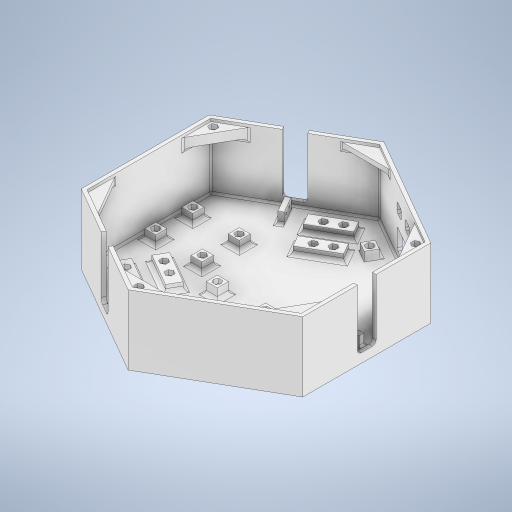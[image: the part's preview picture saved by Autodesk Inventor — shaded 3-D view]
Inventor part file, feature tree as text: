
AUTODESK INVENTOR PART (.ipt)
format: ipt  version: 2023 (Build 270158000, 158)  size: 2,672,128 bytes
history: native  units: mm
features: extrude x37, sketch x32, fillet x14, mirror x3, other x1
ambient origin geometry x8: Origin, YZ Plane, XZ Plane, XY Plane, X Axis, Y Axis, Z Axis, Center Point
bodies: Body1 (feature_tree)
feature tree (87):
  other  "Bryła1"
  extrude  "Wyciągnięcie proste1"  Depth=239.0mm
  sketch  "Szkic2"
  extrude  "Wyciągnięcie proste3"  Depth=5.0mm TaperAngle=0.0deg
  extrude  "Wyciągnięcie proste5"  Depth=4.0mm
  extrude  "Wyciągnięcie proste6"  Depth=20.0mm
  sketch  "Szkic3"
  extrude  "Wyciągnięcie proste7"  Depth=10.0mm
  extrude  "Wyciągnięcie proste9"  Depth=40.0mm
  extrude  "Wyciągnięcie proste10"  Depth=20.0mm
  mirror  "Odbij2"
  mirror  "Odbij3"
  extrude  "Wyciągnięcie proste11"  Depth=20.0mm
  extrude  "Wyciągnięcie proste12"  Depth=10.0mm
  extrude  "Wyciągnięcie proste13"  Depth=20.0mm
  extrude  "Wyciągnięcie proste16"  Depth=10.0mm
  extrude  "Wyciągnięcie proste17"  Depth=20.0mm
  extrude  "Wyciągnięcie proste18"  Depth=40.0mm
  extrude  "Wyciągnięcie proste22"  Depth=40.0mm
  extrude  "Wyciągnięcie proste23"  Depth=20.0mm
  extrude  "Wyciągnięcie proste24"  Depth=70.0mm TaperAngle=0.0deg
  extrude  "Wyciągnięcie proste25"  Depth=5.0mm TaperAngle=0.0deg
  extrude  "Wyciągnięcie proste28"  Depth=70.0mm TaperAngle=0.0deg
  extrude  "Wyciągnięcie proste29"  Depth=15.0mm
  fillet  "Zaokrąglenie1"  Radius=8.0mm
  fillet  "Zaokrąglenie2"  [1 undecoded]
  fillet  "Zaokrąglenie4"  Radius=15.0mm
  fillet  "Zaokrąglenie5"  Radius=8.0mm
  extrude  "Wyciągnięcie proste30"  Depth=3.0mm TaperAngle=0.0deg
  mirror  "Odbij4"
  extrude  "Wyciągnięcie proste31"  Depth=50.0mm
  extrude  "Wyciągnięcie proste32"  Depth=50.0mm
  extrude  "Wyciągnięcie proste33"  Depth=50.0mm
  fillet  "Zaokrąglenie6"  Radius=50.0mm
  fillet  "Zaokrąglenie7"  Radius=50.0mm
  fillet  "Zaokrąglenie8"  Radius=50.0mm
  fillet  "Zaokrąglenie9"  Radius=14.0mm
  extrude  "Wyciągnięcie proste34"  Depth=40.0mm
  extrude  "Wyciągnięcie proste35"  Depth=3.0mm
  fillet  "Zaokrąglenie10"  Radius=14.0mm
  fillet  "Zaokrąglenie11"  Radius=40.0mm
  extrude  "Wyciągnięcie proste36"  Depth=3.0mm
  extrude  "Wyciągnięcie proste37"  Depth=5.0mm
  extrude  "Wyciągnięcie proste38"  Depth=5.0mm
  fillet  "Zaokrąglenie12"  Radius=8.0mm
  extrude  "Wyciągnięcie proste39"  Depth=14.0mm
  sketch  "Szkic45"
  extrude  "Wyciągnięcie proste40"  Depth=14.0mm
  extrude  "Wyciągnięcie proste41"  Depth=5.0mm
  fillet  "Zaokrąglenie13"  Radius=40.0mm
  extrude  "Wyciągnięcie proste42"  Depth=3.0mm
  extrude  "Wyciągnięcie proste43"  Depth=3.0mm
  extrude  "Wyciągnięcie proste44"  Depth=3.0mm
  extrude  "Wyciągnięcie proste45"  Depth=14.0mm
  extrude  "Wyciągnięcie proste46"  Depth=14.0mm
  extrude  "Wyciągnięcie proste47"  Depth=16.0mm
  fillet  "Zaokrąglenie14"  Radius=5.0mm
  fillet  "Zaokrąglenie15"  Radius=5.0mm
  sketch  "Szkic4"
  sketch  "Szkic6"
  sketch  "Szkic15"
  sketch  "Szkic16"
  sketch  "Szkic19"
  sketch  "Szkic20"
  sketch  "Szkic21"
  sketch  "Szkic27"
  sketch  "Szkic28"
  sketch  "Szkic29"
  sketch  "Szkic30"
  sketch  "Szkic33"
  sketch  "Szkic34"
  sketch  "Szkic35"
  sketch  "Szkic36"
  sketch  "Szkic37"
  sketch  "Szkic38"
  sketch  "Szkic39"
  sketch  "Szkic40"
  sketch  "Szkic41"
  sketch  "Szkic42"
  sketch  "Szkic43"
  sketch  "Szkic44"
  sketch  "Szkic46"
  sketch  "Szkic47"
  sketch  "Szkic48"
  sketch  "Szkic49"
  sketch  "Szkic50"
  sketch  "Szkic51"
note: 1 required parameter value undecoded (feature->parameter linkage not recoverable at this tier; creation-order binding heuristic only, values carry confidence <= 0.55)
